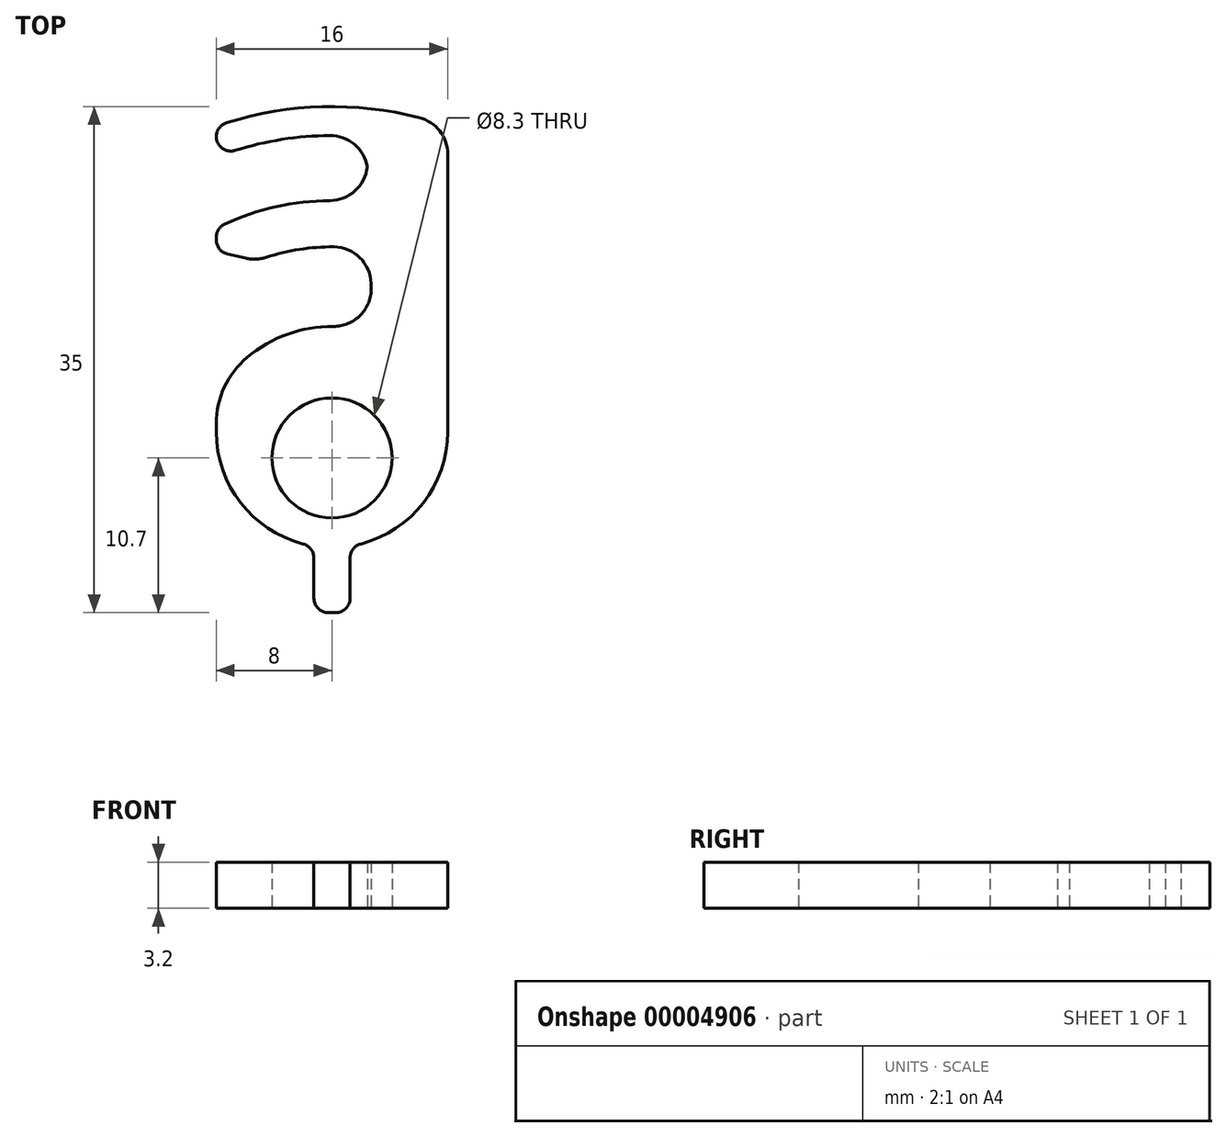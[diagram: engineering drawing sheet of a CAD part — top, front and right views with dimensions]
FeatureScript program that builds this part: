
annotation { "Feature Type Name" : "Feature", "Feature Type Description" : "" }
export const myFeature = defineFeature(function(context is Context, id is Id, definition is map)
    precondition{}
    {
        {
            var Q0;
            Q0=qCreatedBy(makeId("Top.planeOp"),FACE);
            var sketch = newSketch(context, id + "F0", { "sketchPlane" : qUnion([Q0])});
            skArc(sketch, "E0", {"start": v(-8, 0) * mm, "mid": v(-6.08, -5.2) * mm, "end": v(-1.25, -7.9) * mm});
            skLineSegment(sketch, "E1.left", {"start": v(-8, 0) * mm, "end": v(-8, 2.54) * mm});
            skLineSegment(sketch, "E1.right", {"start": v(8, 0) * mm, "end": v(8, 21.15) * mm});
            skCircle(sketch, "E2", {"center": v(0, -1.8) * mm, "radius": 4.15 * mm});
            skLineSegment(sketch, "E3.top", {"start": v(-1.25, -12.5) * mm, "end": v(1.25, -12.5) * mm});
            skLineSegment(sketch, "E3.left", {"start": v(-1.25, -7.9) * mm, "end": v(-1.25, -12.5) * mm});
            skLineSegment(sketch, "E3.right", {"start": v(1.25, -7.9) * mm, "end": v(1.25, -12.5) * mm});
            skArc(sketch, "E4.trimOffspring", {"start": v(1.25, -7.9) * mm, "mid": v(6.08, -5.2) * mm, "end": v(8, 0) * mm});
            skLineSegment(sketch, "E5", {"start": v(0, 0) * mm, "end": v(0, -12.5) * mm, "construction": true});
            skArc(sketch, "E6", {"start": v(8, 21.15) * mm, "mid": v(0, 22.5) * mm, "end": v(-8, 21.15) * mm});
            skArc(sketch, "E7", {"start": v(2.4, 20.37) * mm, "mid": v(-2.88, 20.31) * mm, "end": v(-8, 19.02) * mm});
            skArc(sketch, "E8", {"start": v(2.53, 15.82) * mm, "mid": v(-2.86, 15.77) * mm, "end": v(-8, 14.1) * mm});
            skArc(sketch, "E9", {"start": v(2.8, 6.86) * mm, "mid": v(-3.38, 6.65) * mm, "end": v(-8, 2.54) * mm});
            skLineSegment(sketch, "E10", {"start": v(2.4, 20.37) * mm, "end": v(2.53, 15.82) * mm});
            skLineSegment(sketch, "E11", {"start": v(2.63, 12.56) * mm, "end": v(2.8, 6.86) * mm});
            skLineSegment(sketch, "E12.trimOffspring", {"start": v(-8, 19.02) * mm, "end": v(-8, 21.15) * mm});
            skLineSegment(sketch, "E13.trimOffspring", {"start": v(-8, 10.41) * mm, "end": v(-8, 14.1) * mm});
            skArc(sketch, "E14", {"start": v(2.63, 12.56) * mm, "mid": v(-2.9, 12.51) * mm, "end": v(-8, 10.41) * mm});
            skSolve(sketch);
        }
        {
            var Q0;
            Q0=makeQuery(id+"F0.imprint","IMPRINT",FACE,{"disambiguationData":[TD([[makeQuery(id+"F0.imprint","IMPRINT",EDGE,{"derivedFrom":sQuery(id+"F0.wireOp",EDGE,"E0")}),1.0]])]});
            extrude(context, id + "F1", {"entities" : qUnion([Q0]), "endBound" : BoundingType.SYMMETRIC, "depth" : 3.2 * mm});
        }
        {
            var Q0;
            Q0=makeQuery(id+"F1.opExtrude","SWEPT_EDGE",EDGE,{"disambiguationData":[OSD([sQuery(id+"F0.wireOp",EDGE,"E13.trimOffspring"),sQuery(id+"F0.wireOp",EDGE,"E14")])]});
            chamfer(context, id + "F2", {"entities" : qUnion([Q0]), "chamferType" : ChamferType.TWO_OFFSETS, "width1" : 2.5 * mm, "oppositeDirection" : true, "width2" : 3.5 * mm, "tangentPropagation" : true});
        }
        {
            var Q0;
            Q0=makeQuery(id+"F1.opExtrude","SWEPT_EDGE",EDGE,{"disambiguationData":[OSD([sQuery(id+"F0.wireOp",EDGE,"E7"),sQuery(id+"F0.wireOp",EDGE,"E10")])]});
            var Q1;
            Q1=makeQuery(id+"F1.opExtrude","SWEPT_EDGE",EDGE,{"disambiguationData":[OSD([sQuery(id+"F0.wireOp",EDGE,"E8"),sQuery(id+"F0.wireOp",EDGE,"E10")])]});
            var Q2;
            Q2=makeQuery(id+"F1.opExtrude","SWEPT_EDGE",EDGE,{"disambiguationData":[OSD([sQuery(id+"F0.wireOp",EDGE,"E11"),sQuery(id+"F0.wireOp",EDGE,"E14")])]});
            var Q3;
            Q3=makeQuery(id+"F1.opExtrude","SWEPT_EDGE",EDGE,{"disambiguationData":[OSD([sQuery(id+"F0.wireOp",EDGE,"E9"),sQuery(id+"F0.wireOp",EDGE,"E11")])]});
            var Q4;
            Q4=makeQuery(id+"F1.opExtrude","SWEPT_EDGE",EDGE,{"disambiguationData":[OSD([sQuery(id+"F0.wireOp",EDGE,"E1.right"),sQuery(id+"F0.wireOp",EDGE,"E6")])]});
            var Q5;
            {var subQ0=sQuery(id+"F0.wireOp",EDGE,"E14");Q5=makeQuery(id+"F2.opChamfer","BLEND_EDGE",EDGE,{"blendedFrom":[makeQuery(id+"F1.opExtrude","SWEPT_EDGE",EDGE,{"disambiguationData":[OSD([sQuery(id+"F0.wireOp",EDGE,"E13.trimOffspring"),subQ0])]}),makeQuery(id+"F1.opExtrude","SWEPT_FACE",FACE,{"disambiguationData":[OSD([subQ0])]})],"blendedInto":[makeQuery(id+"F1.opExtrude","SWEPT_FACE",FACE,{"disambiguationData":[OSD([subQ0])]})]});}
            fillet(context, id + "F3", {"entities" : qUnion([Q0, Q1, Q2, Q3, Q4, Q5]), "radius" : 2.6 * mm, "tangentPropagation" : true, "allowEdgeOverflow" : false});
        }
        {
            var Q0;
            Q0=makeQuery(id+"F1.opExtrude","SWEPT_EDGE",EDGE,{"disambiguationData":[OSD([sQuery(id+"F0.wireOp",EDGE,"E7"),sQuery(id+"F0.wireOp",EDGE,"E12.trimOffspring")])]});
            var Q1;
            Q1=makeQuery(id+"F1.opExtrude","SWEPT_EDGE",EDGE,{"disambiguationData":[OSD([sQuery(id+"F0.wireOp",EDGE,"E6"),sQuery(id+"F0.wireOp",EDGE,"E12.trimOffspring")])]});
            var Q2;
            Q2=makeQuery(id+"F1.opExtrude","SWEPT_EDGE",EDGE,{"disambiguationData":[OSD([sQuery(id+"F0.wireOp",EDGE,"E8"),sQuery(id+"F0.wireOp",EDGE,"E13.trimOffspring")])]});
            var Q3;
            Q3=makeQuery(id+"F1.opExtrude","SWEPT_EDGE",EDGE,{"disambiguationData":[OSD([sQuery(id+"F0.wireOp",EDGE,"E3.top"),sQuery(id+"F0.wireOp",EDGE,"E3.left")])]});
            var Q4;
            Q4=makeQuery(id+"F1.opExtrude","SWEPT_EDGE",EDGE,{"disambiguationData":[OSD([sQuery(id+"F0.wireOp",EDGE,"E3.top"),sQuery(id+"F0.wireOp",EDGE,"E3.right")])]});
            var Q5;
            {var subQ0=sQuery(id+"F0.wireOp",EDGE,"E13.trimOffspring");Q5=makeQuery(id+"F2.opChamfer","BLEND_EDGE",EDGE,{"blendedFrom":[makeQuery(id+"F1.opExtrude","SWEPT_EDGE",EDGE,{"disambiguationData":[OSD([subQ0,sQuery(id+"F0.wireOp",EDGE,"E14")])]}),makeQuery(id+"F1.opExtrude","SWEPT_FACE",FACE,{"disambiguationData":[OSD([subQ0])]})],"blendedInto":[makeQuery(id+"F1.opExtrude","SWEPT_FACE",FACE,{"disambiguationData":[OSD([subQ0])]})]});}
            var Q6;
            Q6=makeQuery(id+"F1.opExtrude","SWEPT_EDGE",EDGE,{"disambiguationData":[OSD([sQuery(id+"F0.wireOp",EDGE,"E0"),sQuery(id+"F0.wireOp",EDGE,"E3.left")])]});
            var Q7;
            Q7=makeQuery(id+"F1.opExtrude","SWEPT_EDGE",EDGE,{"disambiguationData":[OSD([sQuery(id+"F0.wireOp",EDGE,"E3.right"),sQuery(id+"F0.wireOp",EDGE,"E4.trimOffspring")])]});
            fillet(context, id + "F4", {"entities" : qUnion([Q0, Q1, Q2, Q3, Q4, Q5, Q6, Q7]), "radius" : 1 * mm, "tangentPropagation" : true, "allowEdgeOverflow" : false});
        }
        {
            var Q0;
            Q0=makeQuery(id+"F1.opExtrude","SWEPT_EDGE",EDGE,{"disambiguationData":[OSD([sQuery(id+"F0.wireOp",EDGE,"E1.left"),sQuery(id+"F0.wireOp",EDGE,"E9")])]});
            fillet(context, id + "F5", {"entities" : qUnion([Q0]), "radius" : 6 * mm, "tangentPropagation" : true, "allowEdgeOverflow" : false});
        }
    });
